# Revit family: ITK_Патч-панель 19-дюймовое крепление_2U_категория 5E UTP GENERICA_48 портов
name_source: partatom
category: Обобщенные модели
units: mm (PartAtom-declared; Revit-internal decimal feet)

## family parameters
Всегда вертикально = Да
Может служить основой для арматурных стержней = Нет
На основе рабочей плоскости = Нет
Общий = Нет
При загрузке вырезать с полостями = Нет
Размер круглого соединителя = Использовать диаметр
Тип детали = Нормальный
Точка расчета площади = Нет

## types (1)
- PP48-2UC5EU-K05-G
    ADSK_URL страницы изделия = https://generica.su
    ADSK_Версия Revit = 2019
    ADSK_Версия семейства = 1.0
    ADSK_Группирование = I. ЩИТЫ И ПУЛЬТЫ
    ADSK_Единица измерения = шт
    ADSK_Завод-изготовитель = IEK
    ADSK_Код изделия = PP48-2UC5EU-K05-G
    ADSK_Масса = 0
    ADSK_Материал наименование = Металл и АБС-пластик
    ADSK_Наименование = Патч-панель 2U кат. 5Е UTP 48 портов (Krone) GENERICA
    IEK_URL = https://generica.su
    IEK_Описание = Патч-панели для монтажа в 19" шкаф или стойку соответствуют стандарту 19" (482,6 мм), имеют отверстия с левой и правой стороны для крепления на профиль, производятся высотой 1 или 2 юнита.
На передней стороне все патч-панели ITK имеют специальную площадку для дополнительной маркировки и цифровую нумерацию портов, на обратной стороне модули IDC имеют цветовую и цифровую нумерацию. Патч-панели соответствуют международным стандартам. Поставляются в картонной коробке с крепежом.
    IEK_Цена за единицу = 3690.22
    KSI_CMa_Строительные материалы = 10.03.02.06
    KSI_CPr_Строительные изделия = 27.12.31.61.1.04.09-1090
    URL = https://www.iek.ru
    Высота = 88 мм
    Глубина = 37 мм
    Изготовитель = ITK
    Материал = Окраска - RAL 9005
    Ширина = 483 мм
